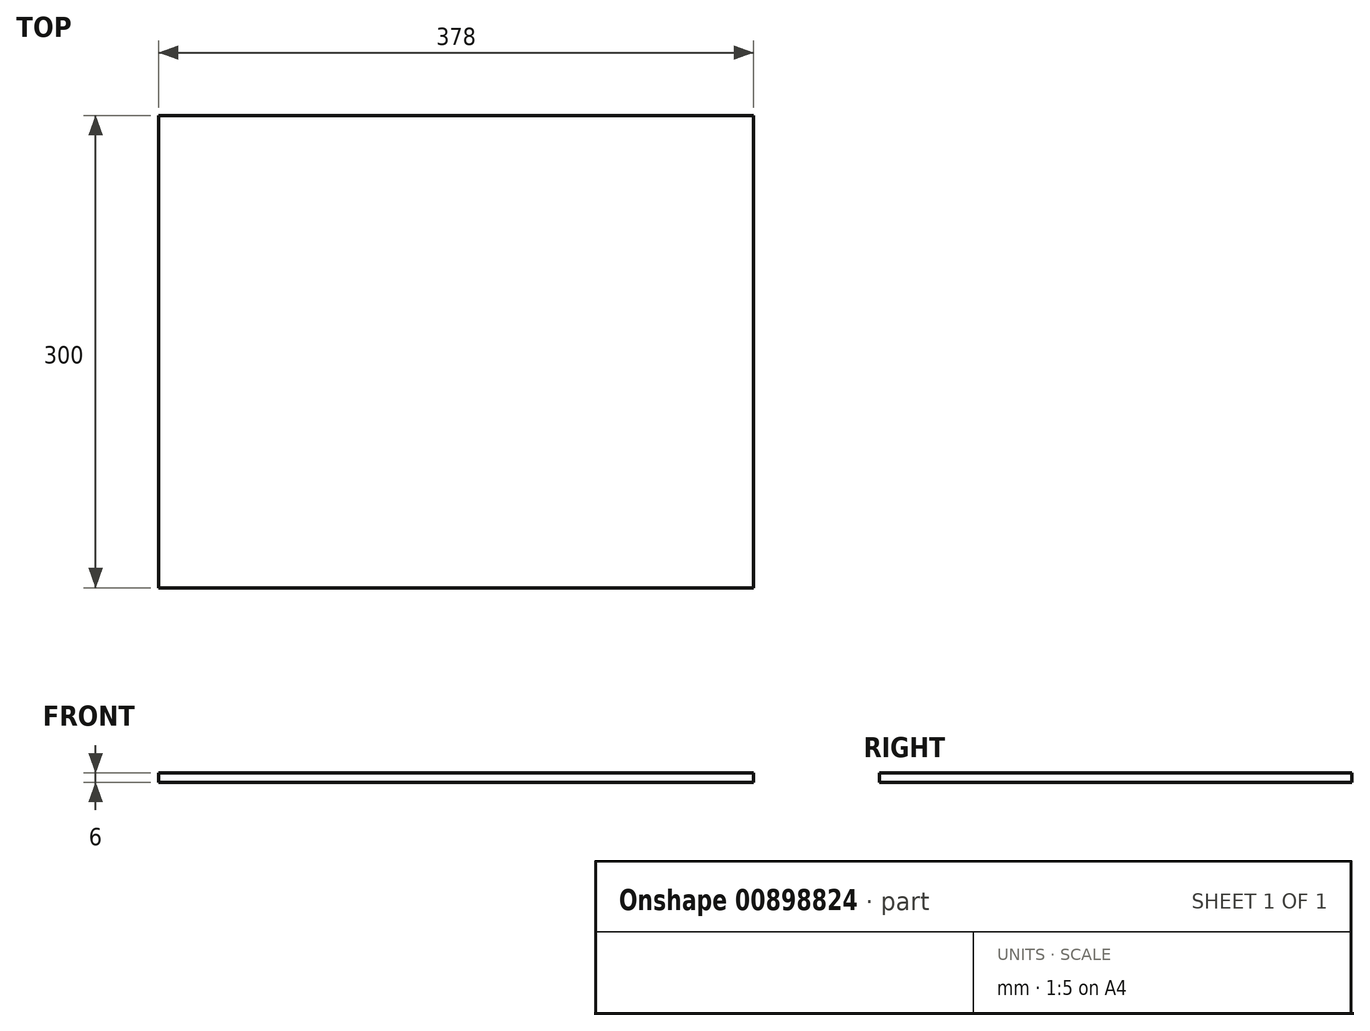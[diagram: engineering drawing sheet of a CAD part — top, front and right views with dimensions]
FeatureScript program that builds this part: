
annotation { "Feature Type Name" : "Feature", "Feature Type Description" : "" }
export const myFeature = defineFeature(function(context is Context, id is Id, definition is map)
    precondition{}
    {
        {
            var Q0;
            Q0=qCreatedBy(makeId("Top.planeOp"),FACE);
            var sketch = newSketch(context, id + "F0", { "sketchPlane" : qUnion([Q0])});
            skLineSegment(sketch, "E0.bottom", {"start": v(189, -150) * mm, "end": v(-189, -150) * mm});
            skLineSegment(sketch, "E0.top", {"start": v(189, 150) * mm, "end": v(-189, 150) * mm});
            skLineSegment(sketch, "E0.left", {"start": v(189, -150) * mm, "end": v(189, 150) * mm});
            skLineSegment(sketch, "E0.right", {"start": v(-189, -150) * mm, "end": v(-189, 150) * mm});
            skPoint(sketch, "E0.middle", {"position": v(0, 0) * mm});
            skSolve(sketch);
        }
        {
            var Q0;
            Q0=makeQuery(id+"F0.imprint","IMPRINT",FACE,{"disambiguationData":[TD([[makeQuery(id+"F0.imprint","IMPRINT",EDGE,{"derivedFrom":sQuery(id+"F0.wireOp",EDGE,"E0.bottom")}),-1.0]])]});
            extrude(context, id + "F1", {"entities" : qUnion([Q0]), "depth" : 6 * mm, "offsetDistance" : 25 * mm});
        }
    });
